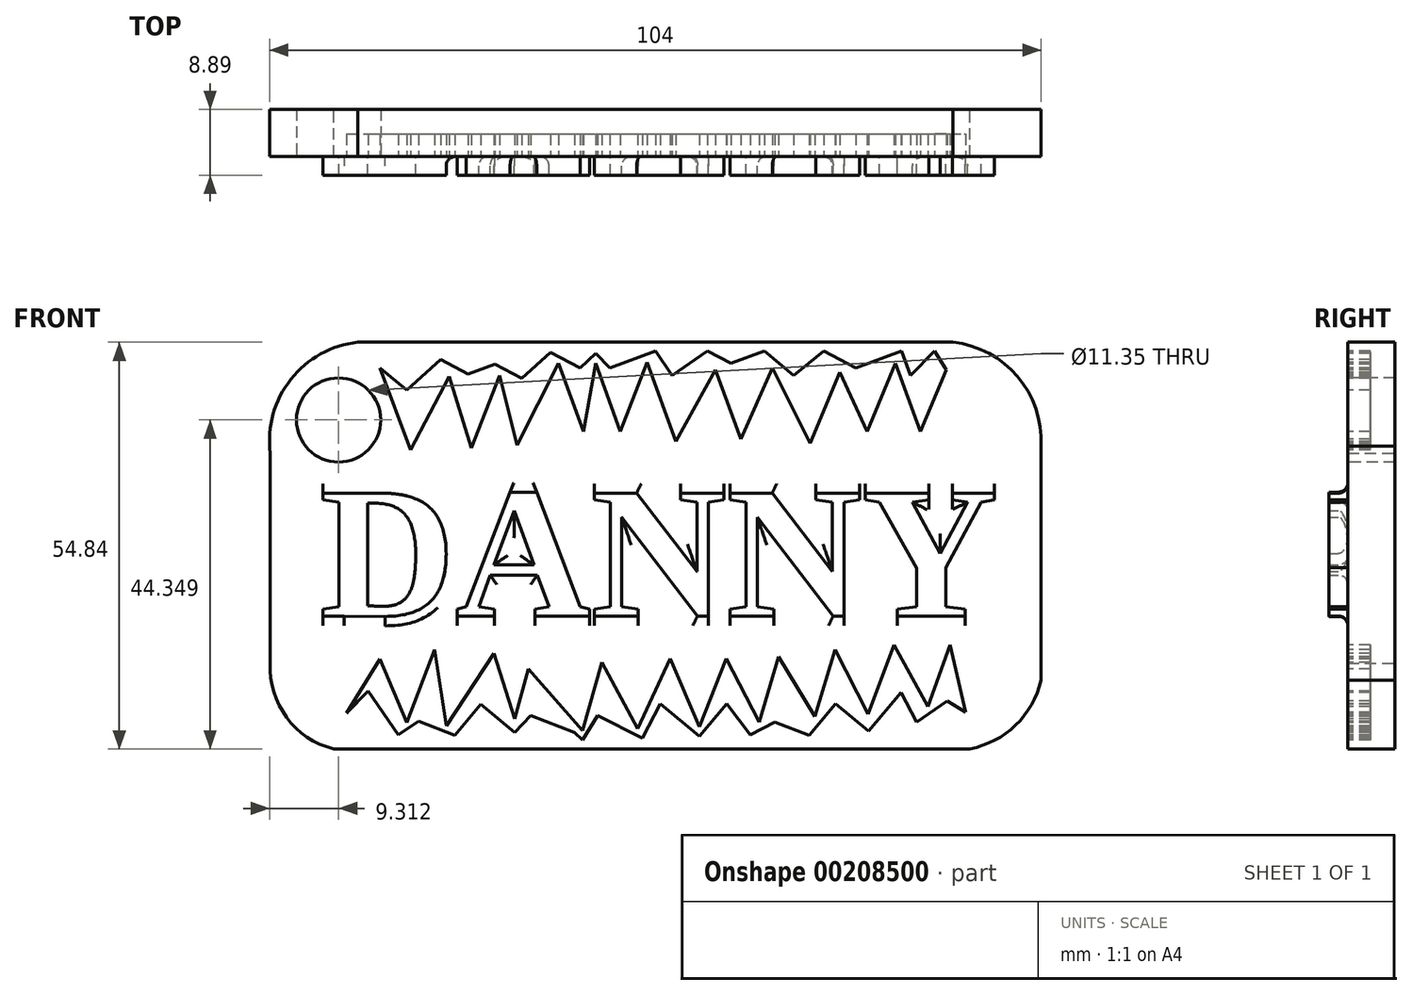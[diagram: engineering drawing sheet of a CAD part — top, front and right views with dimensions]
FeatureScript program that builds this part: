
annotation { "Feature Type Name" : "Feature", "Feature Type Description" : "" }
export const myFeature = defineFeature(function(context is Context, id is Id, definition is map)
    precondition{}
    {
        {
            var Q0;
            Q0=qCreatedBy(makeId("Front.planeOp"),FACE);
            var sketch = newSketch(context, id + "F0", { "sketchPlane" : qUnion([Q0])});
            skLineSegment(sketch, "E0.bottom", {"start": v(-40.09, 25.76) * mm, "end": v(40.09, 25.76) * mm});
            skLineSegment(sketch, "E0.top", {"start": v(-43.34, -29.08) * mm, "end": v(42.4, -29.08) * mm});
            skLineSegment(sketch, "E0.left", {"start": v(-51.9, 14.08) * mm, "end": v(-51.9, -18.65) * mm});
            skLineSegment(sketch, "E0.right", {"start": v(51.98, 13.15) * mm, "end": v(51.98, -19.84) * mm});
            skArc(sketch, "E1", {"start": v(-40.09, 25.76) * mm, "mid": v(-49.11, 20.75) * mm, "end": v(-51.9, 10.8) * mm});
            skArc(sketch, "E2.MirrorCS", {"start": v(40.09, 25.76) * mm, "mid": v(48.82, 21.11) * mm, "end": v(51.98, 11.74) * mm});
            skArc(sketch, "E3", {"start": v(-51.9, -17.52) * mm, "mid": v(-49.69, -24.83) * mm, "end": v(-43.34, -29.08) * mm});
            skArc(sketch, "E4", {"start": v(42.4, -29.08) * mm, "mid": v(48.55, -25.87) * mm, "end": v(51.98, -19.84) * mm});
            skPoint(sketch, "E5.orphan", {"position": v(37.1, 25.76) * mm});
            skPoint(sketch, "E6.orphan", {"position": v(-37.1, 25.76) * mm});
            skPoint(sketch, "E7.orphan", {"position": v(-6.83, 0) * mm});
            skPoint(sketch, "E8.start.orphan", {"position": v(0, -4.35) * mm});
            skSolve(sketch);
        }
        {
            var Q0;
            Q0 = qSketchRegion(id + "F0", true);
            extrude(context, id + "F1", {"entities" : qUnion([Q0]), "depth" : 6.35 * mm});
        }
        {
            var Q0;
            Q0=makeQuery(id+"F1.opExtrude","CAP_FACE",FACE,{"disambiguationData":[OSD([sQuery(id+"F0.wireOp",EDGE,"E0.bottom"),sQuery(id+"F0.wireOp",EDGE,"E0.top"),sQuery(id+"F0.wireOp",EDGE,"E0.left"),sQuery(id+"F0.wireOp",EDGE,"E0.right"),sQuery(id+"F0.wireOp",EDGE,"E1"),sQuery(id+"F0.wireOp",EDGE,"E2.MirrorCS"),sQuery(id+"F0.wireOp",EDGE,"E3"),sQuery(id+"F0.wireOp",EDGE,"E4")])],"isStart":false});
            var sketch = newSketch(context, id + "F2", { "sketchPlane" : qUnion([Q0])});
            skText(sketch, "E9", { "text": "DANNY", "fontName": "Tinos-Bold.ttf"});
            const initialGuessF2  = {"E9": [-0.04523, -0.01116, 1, 0, 0.01822]};
            skSetInitialGuess(sketch, initialGuessF2);
            skSolve(sketch);
        }
        {
            var Q0;
            Q0 = qSketchRegion(id + "F2", true);
            extrude(context, id + "F3", {"entities" : qUnion([Q0]), "operationType" : NewBodyOperationType.ADD, "depth" : 2.54 * mm});
        }
        {
            var Q0;
            {var subQ0=sQuery(id+"F0.wireOp",EDGE,"E3");var subQ1=sQuery(id+"F0.wireOp",EDGE,"E4");var subQ2=sQuery(id+"F0.wireOp",EDGE,"E0.left");var subQ3=sQuery(id+"F0.wireOp",EDGE,"E0.right");var subQ4=sQuery(id+"F0.wireOp",EDGE,"E2.MirrorCS");var subQ5=sQuery(id+"F0.wireOp",EDGE,"E0.top");var subQ6=sQuery(id+"F0.wireOp",EDGE,"E0.bottom");var subQ7=sQuery(id+"F0.wireOp",EDGE,"E1");Q0=makeQuery(id+"F3.boolean.opBoolean","SPLIT",FACE,{"disambiguationData":[TD([makeQuery(id+"F1.opExtrude","SWEPT_FACE",FACE,{"disambiguationData":[OSD([subQ6])]})])],"derivedFrom":makeQuery(id+"F1.opExtrude","CAP_FACE",FACE,{"disambiguationData":[OSD([subQ6,subQ5,subQ2,subQ3,subQ7,subQ4,subQ0,subQ1])],"isStart":false})});}
            var sketch = newSketch(context, id + "F4", { "sketchPlane" : qUnion([Q0])});
            skLineSegment(sketch, "E10", {"start": v(-37.1, 22.29) * mm, "end": v(-33, 11.25) * mm});
            skLineSegment(sketch, "E11", {"start": v(-33, 11.25) * mm, "end": v(-27.79, 21.17) * mm});
            skLineSegment(sketch, "E12", {"start": v(-27.79, 21.17) * mm, "end": v(-24.81, 11.5) * mm});
            skLineSegment(sketch, "E13", {"start": v(-24.81, 11.5) * mm, "end": v(-20.96, 21.3) * mm});
            skLineSegment(sketch, "E14", {"start": v(-20.96, 21.3) * mm, "end": v(-18.6, 11.87) * mm});
            skLineSegment(sketch, "E15", {"start": v(-18.6, 11.87) * mm, "end": v(-13.02, 22.9) * mm});
            skLineSegment(sketch, "E16", {"start": v(-13.02, 22.9) * mm, "end": v(-9.68, 13.73) * mm});
            skLineSegment(sketch, "E17", {"start": v(-9.68, 13.73) * mm, "end": v(-8.06, 22.9) * mm});
            skLineSegment(sketch, "E18", {"start": v(-8.06, 22.9) * mm, "end": v(-4.71, 13.73) * mm});
            skLineSegment(sketch, "E19", {"start": v(-4.71, 13.73) * mm, "end": v(-1.11, 23.03) * mm});
            skLineSegment(sketch, "E20", {"start": v(-1.11, 23.03) * mm, "end": v(2.77, 12.39) * mm});
            skLineSegment(sketch, "E21", {"start": v(2.77, 12.39) * mm, "end": v(8.12, 22.04) * mm});
            skLineSegment(sketch, "E22", {"start": v(8.12, 22.04) * mm, "end": v(11.52, 12.73) * mm});
            skLineSegment(sketch, "E23", {"start": v(11.52, 12.73) * mm, "end": v(15.76, 22.29) * mm});
            skLineSegment(sketch, "E24", {"start": v(15.76, 22.29) * mm, "end": v(20.84, 12.11) * mm});
            skLineSegment(sketch, "E25", {"start": v(20.84, 12.11) * mm, "end": v(24.86, 21.73) * mm});
            skLineSegment(sketch, "E26", {"start": v(24.86, 21.73) * mm, "end": v(28.54, 13.73) * mm});
            skLineSegment(sketch, "E27", {"start": v(28.54, 13.73) * mm, "end": v(32.38, 22.9) * mm});
            skLineSegment(sketch, "E28", {"start": v(32.38, 22.9) * mm, "end": v(35.73, 13.73) * mm});
            skLineSegment(sketch, "E29", {"start": v(-41.85, -24.6) * mm, "end": v(-37.11, -16.98) * mm});
            skLineSegment(sketch, "E30", {"start": v(-37.11, -16.98) * mm, "end": v(-33.52, -25.51) * mm});
            skLineSegment(sketch, "E31", {"start": v(-33.52, -25.51) * mm, "end": v(-29.77, -15.68) * mm});
            skLineSegment(sketch, "E32", {"start": v(-29.77, -15.68) * mm, "end": v(-28.16, -25.97) * mm});
            skLineSegment(sketch, "E33", {"start": v(-28.16, -25.97) * mm, "end": v(-21.72, -16.17) * mm});
            skLineSegment(sketch, "E34", {"start": v(-21.72, -16.17) * mm, "end": v(-18.95, -25.04) * mm});
            skLineSegment(sketch, "E35", {"start": v(-18.95, -25.04) * mm, "end": v(-17.1, -18.3) * mm});
            skLineSegment(sketch, "E36", {"start": v(-17.1, -18.3) * mm, "end": v(-9.8, -26.6) * mm});
            skLineSegment(sketch, "E37", {"start": v(-9.8, -26.6) * mm, "end": v(-7.2, -17.41) * mm});
            skLineSegment(sketch, "E38", {"start": v(-7.2, -17.41) * mm, "end": v(-2.36, -26.34) * mm});
            skLineSegment(sketch, "E39", {"start": v(-2.36, -26.34) * mm, "end": v(1.99, -16.92) * mm});
            skLineSegment(sketch, "E40", {"start": v(1.99, -16.92) * mm, "end": v(5.96, -26.1) * mm});
            skLineSegment(sketch, "E41", {"start": v(5.96, -26.1) * mm, "end": v(9.55, -16.92) * mm});
            skLineSegment(sketch, "E42", {"start": v(9.55, -16.92) * mm, "end": v(14.02, -25.48) * mm});
            skLineSegment(sketch, "E43", {"start": v(14.02, -25.48) * mm, "end": v(16.63, -16.67) * mm});
            skLineSegment(sketch, "E44", {"start": v(16.63, -16.67) * mm, "end": v(21.46, -24.73) * mm});
            skLineSegment(sketch, "E45", {"start": v(21.46, -24.73) * mm, "end": v(24.2, -15.68) * mm});
            skLineSegment(sketch, "E46", {"start": v(24.2, -15.68) * mm, "end": v(28.66, -24.36) * mm});
            skLineSegment(sketch, "E47", {"start": v(28.66, -24.36) * mm, "end": v(32.13, -15.05) * mm});
            skLineSegment(sketch, "E48", {"start": v(32.13, -15.05) * mm, "end": v(36.72, -23.37) * mm});
            skLineSegment(sketch, "E49", {"start": v(36.72, -23.37) * mm, "end": v(39.7, -15.05) * mm});
            skLineSegment(sketch, "E50", {"start": v(39.7, -15.05) * mm, "end": v(41.81, -24.11) * mm});
            skLineSegment(sketch, "E51", {"start": v(35.73, 13.73) * mm, "end": v(39.2, 22.04) * mm});
            skLineSegment(sketch, "E52", {"start": v(-37.1, 22.29) * mm, "end": v(-33.5, 19.31) * mm});
            skLineSegment(sketch, "E53", {"start": v(-33.5, 19.31) * mm, "end": v(-28.9, 23.4) * mm});
            skLineSegment(sketch, "E54", {"start": v(-28.9, 23.4) * mm, "end": v(-25.2, 21.46) * mm});
            skLineSegment(sketch, "E55", {"start": v(-25.2, 21.46) * mm, "end": v(-21.64, 22.79) * mm});
            skLineSegment(sketch, "E56", {"start": v(-21.64, 22.79) * mm, "end": v(-18, 20.88) * mm});
            skLineSegment(sketch, "E57", {"start": v(-18, 20.88) * mm, "end": v(-14.14, 24.4) * mm});
            skLineSegment(sketch, "E58", {"start": v(-14.14, 24.4) * mm, "end": v(-10.12, 22.29) * mm});
            skLineSegment(sketch, "E59", {"start": v(-10.12, 22.29) * mm, "end": v(-8.06, 24.27) * mm});
            skLineSegment(sketch, "E60", {"start": v(-8.06, 24.27) * mm, "end": v(-6.15, 22.29) * mm});
            skLineSegment(sketch, "E61", {"start": v(-6.15, 22.29) * mm, "end": v(0, 24.57) * mm});
            skLineSegment(sketch, "E62", {"start": v(0, 24.57) * mm, "end": v(2.23, 21.3) * mm});
            skLineSegment(sketch, "E63", {"start": v(2.23, 21.3) * mm, "end": v(7.03, 24.57) * mm});
            skLineSegment(sketch, "E64", {"start": v(7.03, 24.57) * mm, "end": v(10.2, 22.9) * mm});
            skLineSegment(sketch, "E65", {"start": v(10.2, 22.9) * mm, "end": v(14.67, 24.57) * mm});
            skLineSegment(sketch, "E66", {"start": v(14.67, 24.57) * mm, "end": v(18.61, 21.3) * mm});
            skLineSegment(sketch, "E67", {"start": v(18.61, 21.3) * mm, "end": v(22.7, 24.57) * mm});
            skLineSegment(sketch, "E68", {"start": v(22.7, 24.57) * mm, "end": v(27.05, 22.29) * mm});
            skLineSegment(sketch, "E69", {"start": v(27.05, 22.29) * mm, "end": v(33.2, 24.57) * mm});
            skLineSegment(sketch, "E70", {"start": v(33.2, 24.57) * mm, "end": v(34.41, 21.3) * mm});
            skLineSegment(sketch, "E71", {"start": v(34.41, 21.3) * mm, "end": v(37.6, 24.57) * mm});
            skLineSegment(sketch, "E72", {"start": v(39.2, 22.04) * mm, "end": v(37.6, 24.57) * mm});
            skLineSegment(sketch, "E73", {"start": v(-41.65, -24.29) * mm, "end": v(-38.7, -21.25) * mm});
            skPoint(sketch, "E73.endSnap0", {"position": v(-35.31, -21.25) * mm});
            skLineSegment(sketch, "E74", {"start": v(-38.7, -21.25) * mm, "end": v(-34.61, -27.21) * mm});
            skLineSegment(sketch, "E75", {"start": v(-34.61, -27.21) * mm, "end": v(-31.92, -25.37) * mm});
            skLineSegment(sketch, "E76", {"start": v(-31.92, -25.37) * mm, "end": v(-27.02, -27.23) * mm});
            skLineSegment(sketch, "E77", {"start": v(-27.02, -27.23) * mm, "end": v(-23.55, -23.06) * mm});
            skLineSegment(sketch, "E78", {"start": v(-23.55, -23.06) * mm, "end": v(-18.97, -26.86) * mm});
            skLineSegment(sketch, "E79", {"start": v(-18.97, -26.86) * mm, "end": v(-16.79, -24.6) * mm});
            skLineSegment(sketch, "E80", {"start": v(-16.79, -24.6) * mm, "end": v(-10.87, -26.86) * mm});
            skLineSegment(sketch, "E81", {"start": v(-10.87, -26.86) * mm, "end": v(-9.8, -27.9) * mm});
            skLineSegment(sketch, "E82", {"start": v(-9.8, -27.9) * mm, "end": v(-7.75, -24.6) * mm});
            skLineSegment(sketch, "E83", {"start": v(-7.75, -24.6) * mm, "end": v(-1.76, -27.64) * mm});
            skLineSegment(sketch, "E84", {"start": v(-1.76, -27.64) * mm, "end": v(0.67, -23) * mm});
            skLineSegment(sketch, "E85", {"start": v(0.67, -23) * mm, "end": v(5.94, -27.38) * mm});
            skLineSegment(sketch, "E86", {"start": v(5.94, -27.38) * mm, "end": v(9.61, -22.96) * mm});
            skLineSegment(sketch, "E87", {"start": v(9.61, -22.96) * mm, "end": v(12.78, -27.21) * mm});
            skLineSegment(sketch, "E88", {"start": v(12.78, -27.21) * mm, "end": v(16.1, -25.48) * mm});
            skLineSegment(sketch, "E89", {"start": v(16.1, -25.48) * mm, "end": v(20.7, -27.25) * mm});
            skLineSegment(sketch, "E90", {"start": v(20.7, -27.25) * mm, "end": v(24.27, -22.96) * mm});
            skLineSegment(sketch, "E91", {"start": v(24.27, -22.96) * mm, "end": v(28.75, -26.68) * mm});
            skLineSegment(sketch, "E92", {"start": v(28.75, -26.68) * mm, "end": v(33.1, -21.44) * mm});
            skLineSegment(sketch, "E93", {"start": v(33.1, -21.44) * mm, "end": v(35.2, -25.48) * mm});
            skLineSegment(sketch, "E94", {"start": v(35.2, -25.48) * mm, "end": v(39.33, -22.62) * mm});
            skLineSegment(sketch, "E95", {"start": v(39.33, -22.62) * mm, "end": v(41.81, -24.11) * mm});
            skSolve(sketch);
        }
        {
            var Q0;
            Q0 = qSketchRegion(id + "F4", true);
            extrude(context, id + "F5", {"entities" : qUnion([Q0]), "operationType" : NewBodyOperationType.REMOVE, "oppositeDirection" : true, "depth" : 3.05 * mm});
        }
        {
            var Q0;
            Q0=makeQuery(id+"F3.opExtrude","CAP_EDGE",EDGE,{"disambiguationData":[OSD([sQuery(id+"F2.wireOp",EDGE,"E9.sketch_text.stroke-13")])],"isStart":true});
            var Q1;
            Q1=makeQuery(id+"F3.opExtrude","CAP_EDGE",EDGE,{"disambiguationData":[OSD([sQuery(id+"F2.wireOp",EDGE,"E9.sketch_text.stroke-12")])],"isStart":true});
            var Q2;
            Q2=makeQuery(id+"F3.boolean.opBoolean","SPLIT",FACE,{"disambiguationData":[TD([makeQuery(id+"F3.opExtrude","SWEPT_FACE",FACE,{"disambiguationData":[OSD([sQuery(id+"F2.wireOp",EDGE,"E9.sketch_text.stroke-36")])]})])],"derivedFrom":makeQuery(id+"F1.opExtrude","CAP_FACE",FACE,{"disambiguationData":[OSD([sQuery(id+"F0.wireOp",EDGE,"E0.bottom"),sQuery(id+"F0.wireOp",EDGE,"E0.top"),sQuery(id+"F0.wireOp",EDGE,"E0.left"),sQuery(id+"F0.wireOp",EDGE,"E0.right"),sQuery(id+"F0.wireOp",EDGE,"E1"),sQuery(id+"F0.wireOp",EDGE,"E2.MirrorCS"),sQuery(id+"F0.wireOp",EDGE,"E3"),sQuery(id+"F0.wireOp",EDGE,"E4")])],"isStart":false})});
            var Q3;
            Q3=makeQuery(id+"F3.opExtrude","CAP_EDGE",EDGE,{"disambiguationData":[OSD([sQuery(id+"F2.wireOp",EDGE,"E9.sketch_text.stroke-33")])],"isStart":true});
            var Q4;
            Q4=makeQuery(id+"F3.opExtrude","CAP_EDGE",EDGE,{"disambiguationData":[OSD([sQuery(id+"F2.wireOp",EDGE,"E9.sketch_text.stroke-32")])],"isStart":true});
            var Q5;
            Q5=makeQuery(id+"F3.opExtrude","CAP_EDGE",EDGE,{"disambiguationData":[OSD([sQuery(id+"F2.wireOp",EDGE,"E9.sketch_text.stroke-34")])],"isStart":true});
            var Q6;
            Q6=makeQuery(id+"F3.opExtrude","CAP_EDGE",EDGE,{"disambiguationData":[OSD([sQuery(id+"F2.wireOp",EDGE,"E9.sketch_text.stroke-29")])],"isStart":true});
            var Q7;
            Q7=makeQuery(id+"F3.opExtrude","CAP_EDGE",EDGE,{"disambiguationData":[OSD([sQuery(id+"F2.wireOp",EDGE,"E9.sketch_text.stroke-21")])],"isStart":true});
            var Q8;
            Q8=makeQuery(id+"F3.opExtrude","CAP_EDGE",EDGE,{"disambiguationData":[OSD([sQuery(id+"F2.wireOp",EDGE,"E9.sketch_text.stroke-11")])],"isStart":true});
            var Q9;
            Q9=makeQuery(id+"F3.opExtrude","CAP_EDGE",EDGE,{"disambiguationData":[OSD([sQuery(id+"F2.wireOp",EDGE,"E9.sketch_text.stroke-10")])],"isStart":true});
            var Q10;
            Q10=makeQuery(id+"F3.opExtrude","CAP_EDGE",EDGE,{"disambiguationData":[OSD([sQuery(id+"F2.wireOp",EDGE,"E9.sketch_text.stroke-9")])],"isStart":true});
            var Q11;
            Q11=makeQuery(id+"F3.opExtrude","CAP_EDGE",EDGE,{"disambiguationData":[OSD([sQuery(id+"F2.wireOp",EDGE,"E9.sketch_text.stroke-19")])],"isStart":true});
            var Q12;
            Q12=makeQuery(id+"F3.opExtrude","CAP_EDGE",EDGE,{"disambiguationData":[OSD([sQuery(id+"F2.wireOp",EDGE,"E9.sketch_text.stroke-8")])],"isStart":true});
            var Q13;
            Q13=makeQuery(id+"F3.opExtrude","CAP_EDGE",EDGE,{"disambiguationData":[OSD([sQuery(id+"F2.wireOp",EDGE,"E9.sketch_text.stroke-50")])],"isStart":true});
            var Q14;
            Q14=makeQuery(id+"F3.opExtrude","CAP_EDGE",EDGE,{"disambiguationData":[OSD([sQuery(id+"F2.wireOp",EDGE,"E9.sketch_text.stroke-45")])],"isStart":true});
            var Q15;
            Q15=makeQuery(id+"F3.opExtrude","CAP_EDGE",EDGE,{"disambiguationData":[OSD([sQuery(id+"F2.wireOp",EDGE,"E9.sketch_text.stroke-70")])],"isStart":true});
            var Q16;
            Q16=makeQuery(id+"F3.opExtrude","CAP_EDGE",EDGE,{"disambiguationData":[OSD([sQuery(id+"F2.wireOp",EDGE,"E9.sketch_text.stroke-65")])],"isStart":true});
            var Q17;
            Q17=makeQuery(id+"F3.opExtrude","CAP_EDGE",EDGE,{"disambiguationData":[OSD([sQuery(id+"F2.wireOp",EDGE,"E9.sketch_text.stroke-67")])],"isStart":true});
            var Q18;
            Q18=makeQuery(id+"F3.opExtrude","CAP_EDGE",EDGE,{"disambiguationData":[OSD([sQuery(id+"F2.wireOp",EDGE,"E9.sketch_text.stroke-66")])],"isStart":true});
            var Q19;
            Q19=makeQuery(id+"F3.opExtrude","CAP_EDGE",EDGE,{"disambiguationData":[OSD([sQuery(id+"F2.wireOp",EDGE,"E9.sketch_text.stroke-46")])],"isStart":true});
            var Q20;
            Q20=makeQuery(id+"F3.opExtrude","CAP_EDGE",EDGE,{"disambiguationData":[OSD([sQuery(id+"F2.wireOp",EDGE,"E9.sketch_text.stroke-47")])],"isStart":true});
            var Q21;
            Q21=makeQuery(id+"F3.opExtrude","CAP_EDGE",EDGE,{"disambiguationData":[OSD([sQuery(id+"F2.wireOp",EDGE,"E9.sketch_text.stroke-57")])],"isStart":true});
            var Q22;
            Q22=makeQuery(id+"F3.opExtrude","CAP_EDGE",EDGE,{"disambiguationData":[OSD([sQuery(id+"F2.wireOp",EDGE,"E9.sketch_text.stroke-58")])],"isStart":true});
            var Q23;
            Q23=makeQuery(id+"F3.opExtrude","CAP_EDGE",EDGE,{"disambiguationData":[OSD([sQuery(id+"F2.wireOp",EDGE,"E9.sketch_text.stroke-78")])],"isStart":true});
            var Q24;
            Q24=makeQuery(id+"F3.opExtrude","CAP_EDGE",EDGE,{"disambiguationData":[OSD([sQuery(id+"F2.wireOp",EDGE,"E9.sketch_text.stroke-77")])],"isStart":true});
            var Q25;
            Q25=makeQuery(id+"F3.opExtrude","CAP_EDGE",EDGE,{"disambiguationData":[OSD([sQuery(id+"F2.wireOp",EDGE,"E9.sketch_text.stroke-25")])],"isStart":true});
            var Q26;
            Q26=makeQuery(id+"F3.opExtrude","CAP_EDGE",EDGE,{"disambiguationData":[OSD([sQuery(id+"F2.wireOp",EDGE,"E9.sketch_text.stroke-56")])],"isStart":true});
            var Q27;
            Q27=makeQuery(id+"F3.opExtrude","CAP_EDGE",EDGE,{"disambiguationData":[OSD([sQuery(id+"F2.wireOp",EDGE,"E9.sketch_text.stroke-41")])],"isStart":true});
            var Q28;
            Q28=makeQuery(id+"F3.opExtrude","CAP_EDGE",EDGE,{"disambiguationData":[OSD([sQuery(id+"F2.wireOp",EDGE,"E9.sketch_text.stroke-76")])],"isStart":true});
            var Q29;
            Q29=makeQuery(id+"F3.opExtrude","CAP_EDGE",EDGE,{"disambiguationData":[OSD([sQuery(id+"F2.wireOp",EDGE,"E9.sketch_text.stroke-61")])],"isStart":true});
            var Q30;
            Q30=makeQuery(id+"F3.opExtrude","CAP_EDGE",EDGE,{"disambiguationData":[OSD([sQuery(id+"F2.wireOp",EDGE,"E9.sketch_text.stroke-89")])],"isStart":true});
            var Q31;
            Q31=makeQuery(id+"F3.opExtrude","CAP_EDGE",EDGE,{"disambiguationData":[OSD([sQuery(id+"F2.wireOp",EDGE,"E9.sketch_text.stroke-96")])],"isStart":true});
            var Q32;
            Q32=makeQuery(id+"F3.opExtrude","CAP_EDGE",EDGE,{"disambiguationData":[OSD([sQuery(id+"F2.wireOp",EDGE,"E9.sketch_text.stroke-91")])],"isStart":true});
            var Q33;
            Q33=makeQuery(id+"F3.opExtrude","CAP_EDGE",EDGE,{"disambiguationData":[OSD([sQuery(id+"F2.wireOp",EDGE,"E9.sketch_text.stroke-94")])],"isStart":true});
            var Q34;
            Q34=makeQuery(id+"F3.opExtrude","CAP_EDGE",EDGE,{"disambiguationData":[OSD([sQuery(id+"F2.wireOp",EDGE,"E9.sketch_text.stroke-92")])],"isStart":true});
            var Q35;
            Q35=makeQuery(id+"F3.opExtrude","CAP_EDGE",EDGE,{"disambiguationData":[OSD([sQuery(id+"F2.wireOp",EDGE,"E9.sketch_text.stroke-93")])],"isStart":true});
            var Q36;
            Q36=makeQuery(id+"F3.opExtrude","CAP_EDGE",EDGE,{"disambiguationData":[OSD([sQuery(id+"F2.wireOp",EDGE,"E9.sketch_text.stroke-82")])],"isStart":true});
            fillet(context, id + "F6", {"entities" : qUnion([Q0, Q1, Q2, Q3, Q4, Q5, Q6, Q7, Q8, Q9, Q10, Q11, Q12, Q13, Q14, Q15, Q16, Q17, Q18, Q19, Q20, Q21, Q22, Q23, Q24, Q25, Q26, Q27, Q28, Q29, Q30, Q31, Q32, Q33, Q34, Q35, Q36]), "radius" : 1.27 * mm, "tangentPropagation" : true, "allowEdgeOverflow" : false});
        }
        {
            var Q0;
            {var subQ0=sQuery(id+"F0.wireOp",EDGE,"E3");var subQ1=sQuery(id+"F0.wireOp",EDGE,"E4");var subQ2=sQuery(id+"F0.wireOp",EDGE,"E0.left");var subQ3=sQuery(id+"F0.wireOp",EDGE,"E0.right");var subQ4=sQuery(id+"F0.wireOp",EDGE,"E2.MirrorCS");var subQ5=sQuery(id+"F0.wireOp",EDGE,"E0.top");var subQ6=sQuery(id+"F0.wireOp",EDGE,"E0.bottom");var subQ7=sQuery(id+"F0.wireOp",EDGE,"E1");Q0=makeQuery(id+"F3.boolean.opBoolean","SPLIT",FACE,{"disambiguationData":[TD([makeQuery(id+"F1.opExtrude","SWEPT_FACE",FACE,{"disambiguationData":[OSD([subQ6])]})])],"derivedFrom":makeQuery(id+"F1.opExtrude","CAP_FACE",FACE,{"disambiguationData":[OSD([subQ6,subQ5,subQ2,subQ3,subQ7,subQ4,subQ0,subQ1])],"isStart":false})});}
            var sketch = newSketch(context, id + "F7", { "sketchPlane" : qUnion([Q0])});
            skCircle(sketch, "E96", {"center": v(-42.69, 15.27) * mm, "radius": 5.68 * mm});
            skSolve(sketch);
        }
        {
            var Q0;
            Q0 = qSketchRegion(id + "F7", true);
            extrude(context, id + "F8", {"entities" : qUnion([Q0]), "operationType" : NewBodyOperationType.REMOVE, "endBound" : BoundingType.THROUGH_ALL, "oppositeDirection" : true, "depth" : 25.4 * mm});
        }
    });
